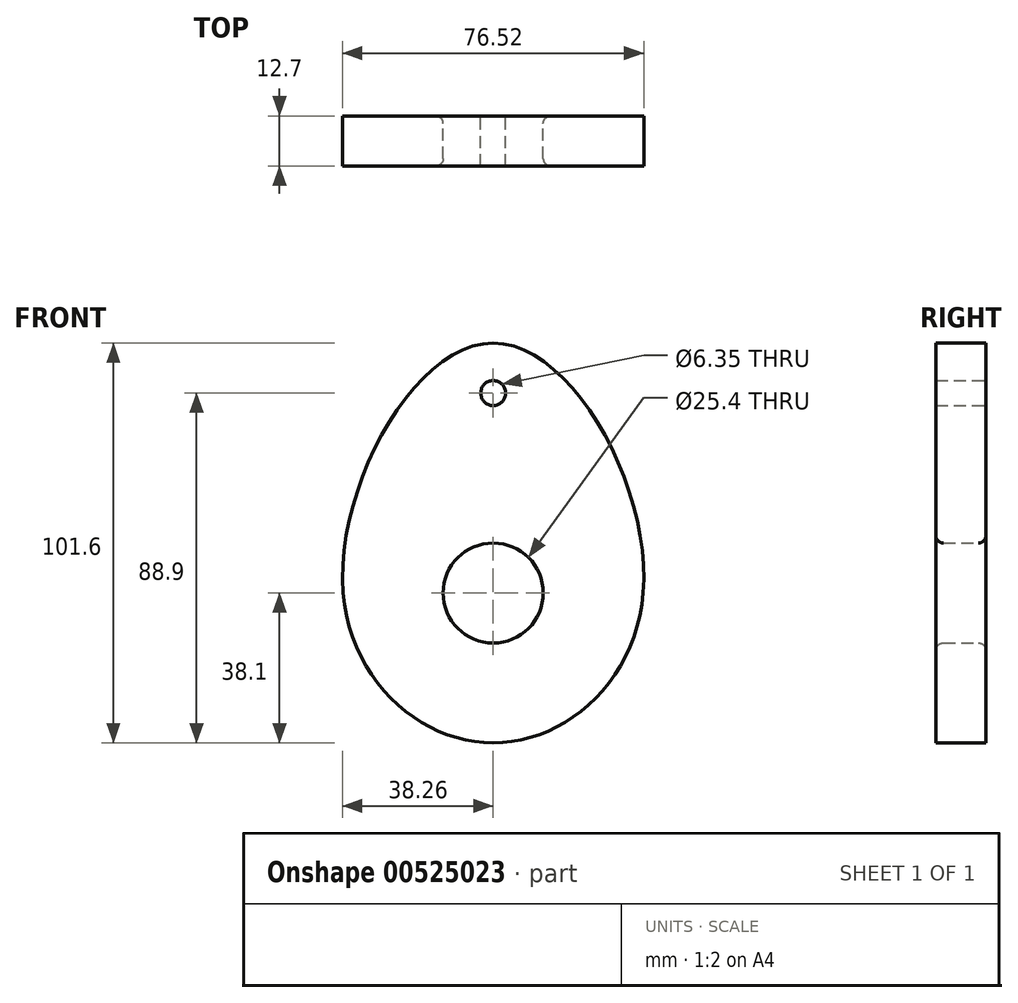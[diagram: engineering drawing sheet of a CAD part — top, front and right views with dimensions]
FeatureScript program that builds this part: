
annotation { "Feature Type Name" : "Feature", "Feature Type Description" : "" }
export const myFeature = defineFeature(function(context is Context, id is Id, definition is map)
    precondition{}
    {
        {
            var Q0;
            Q0=qCreatedBy(makeId("Front.planeOp"),FACE);
            var sketch = newSketch(context, id + "F0", { "sketchPlane" : qUnion([Q0])});
            skLineSegment(sketch, "E0", {"start": v(0, 0) * mm, "end": v(38.1, 0) * mm});
            skLineSegment(sketch, "E1", {"start": v(0, 0) * mm, "end": v(-38.1, 0) * mm});
            skLineSegment(sketch, "E2", {"start": v(0, 0) * mm, "end": v(0, -38.1) * mm});
            skLineSegment(sketch, "E3", {"start": v(0, 0) * mm, "end": v(0, 63.5) * mm});
            skFitSpline(sketch, "E4", {"points": [v(0, 63.5) * mm, v(-38.1, 0) * mm, v(0, -38.1) * mm, v(38.1, 0) * mm, v(0, 63.5) * mm]});
            skLineSegment(sketch, "E5", {"start": v(0, 63.5) * mm, "end": v(0, 50.8) * mm});
            skCircle(sketch, "E6", {"center": v(0, 50.8) * mm, "radius": 3.18 * mm});
            skCircle(sketch, "E7", {"center": v(0, 0) * mm, "radius": 12.7 * mm});
            skCircle(sketch, "E8", {"center": v(0, 0) * mm, "radius": 19.05 * mm});
            skLineSegment(sketch, "E9", {"start": v(0, 0) * mm, "end": v(0, 19.05) * mm});
            skLineSegment(sketch, "E10", {"start": v(0, 0) * mm, "end": v(4.93, 18.4) * mm});
            skLineSegment(sketch, "E11", {"start": v(0, 0) * mm, "end": v(9.52, 16.5) * mm});
            skLineSegment(sketch, "E12", {"start": v(0, 0) * mm, "end": v(13.47, 13.47) * mm});
            skLineSegment(sketch, "E13", {"start": v(0, 0) * mm, "end": v(16.5, 9.53) * mm});
            skLineSegment(sketch, "E14", {"start": v(0, 0) * mm, "end": v(18.4, 4.93) * mm});
            skLineSegment(sketch, "E15", {"start": v(0, 0) * mm, "end": v(19.05, 0) * mm});
            skLineSegment(sketch, "E16", {"start": v(0, 0) * mm, "end": v(18.4, -4.93) * mm});
            skLineSegment(sketch, "E17", {"start": v(0, 0) * mm, "end": v(16.5, -9.52) * mm});
            skLineSegment(sketch, "E18", {"start": v(0, 0) * mm, "end": v(13.47, -13.47) * mm});
            skLineSegment(sketch, "E19", {"start": v(0, 0) * mm, "end": v(9.53, -16.5) * mm});
            skLineSegment(sketch, "E20", {"start": v(0, 0) * mm, "end": v(4.93, -18.4) * mm});
            skLineSegment(sketch, "E21", {"start": v(0, 0) * mm, "end": v(0, -19.05) * mm});
            skLineSegment(sketch, "E22", {"start": v(0, 0) * mm, "end": v(-4.93, -18.4) * mm});
            skLineSegment(sketch, "E23", {"start": v(0, 0) * mm, "end": v(-9.52, -16.5) * mm});
            skLineSegment(sketch, "E24", {"start": v(0, 0) * mm, "end": v(-13.47, -13.47) * mm});
            skLineSegment(sketch, "E25", {"start": v(0, 0) * mm, "end": v(-16.5, -9.53) * mm});
            skLineSegment(sketch, "E26", {"start": v(0, 0) * mm, "end": v(-18.4, -4.93) * mm});
            skLineSegment(sketch, "E27", {"start": v(0, 0) * mm, "end": v(-19.05, 0) * mm});
            skLineSegment(sketch, "E28", {"start": v(0, 0) * mm, "end": v(-13.47, 13.47) * mm});
            skLineSegment(sketch, "E29", {"start": v(0, 0) * mm, "end": v(-16.5, 9.52) * mm});
            skLineSegment(sketch, "E30", {"start": v(0, 0) * mm, "end": v(-18.4, 4.93) * mm});
            skLineSegment(sketch, "E31", {"start": v(0, 0) * mm, "end": v(-4.93, 18.4) * mm});
            skLineSegment(sketch, "E32", {"start": v(0, 0) * mm, "end": v(-9.53, 16.5) * mm});
            skSolve(sketch);
        }
        {
            var Q0;
            Q0 = qSketchRegion(id + "F0", true);
            var Q1;
            {var subQ0=sQuery(id+"F0.wireOp",EDGE,"E30");var subQ1=sQuery(id+"F0.wireOp",EDGE,"E7");var subQ2=makeQuery(id+"F0.imprint","INTERSECT",VERTEX,{"derivedFrom":[subQ1,subQ0]});Q1=makeQuery(id+"F0.imprint","IMPRINT",FACE,{"disambiguationData":[TD([[makeQuery(id+"F0.imprint","IMPRINT",EDGE,{"disambiguationData":[TD([[subQ2,-1.0]])],"derivedFrom":subQ1}),-1.0]])]});}
            var Q2;
            {var subQ0=sQuery(id+"F0.wireOp",EDGE,"E28");var subQ1=sQuery(id+"F0.wireOp",EDGE,"E7");var subQ2=makeQuery(id+"F0.imprint","INTERSECT",VERTEX,{"derivedFrom":[subQ1,subQ0]});Q2=makeQuery(id+"F0.imprint","IMPRINT",FACE,{"disambiguationData":[TD([[makeQuery(id+"F0.imprint","IMPRINT",EDGE,{"disambiguationData":[TD([[subQ2,-1.0]])],"derivedFrom":subQ1}),-1.0]])]});}
            var Q3;
            {var subQ0=sQuery(id+"F0.wireOp",EDGE,"E31");var subQ1=sQuery(id+"F0.wireOp",EDGE,"E7");var subQ2=makeQuery(id+"F0.imprint","INTERSECT",VERTEX,{"derivedFrom":[subQ1,subQ0]});Q3=makeQuery(id+"F0.imprint","IMPRINT",FACE,{"disambiguationData":[TD([[makeQuery(id+"F0.imprint","IMPRINT",EDGE,{"disambiguationData":[TD([[subQ2,-1.0]])],"derivedFrom":subQ1}),-1.0]])]});}
            var Q4;
            {var subQ0=sQuery(id+"F0.wireOp",EDGE,"E10");var subQ1=sQuery(id+"F0.wireOp",EDGE,"E7");var subQ2=makeQuery(id+"F0.imprint","INTERSECT",VERTEX,{"derivedFrom":[subQ1,subQ0]});Q4=makeQuery(id+"F0.imprint","IMPRINT",FACE,{"disambiguationData":[TD([[makeQuery(id+"F0.imprint","IMPRINT",EDGE,{"disambiguationData":[TD([[subQ2,-1.0]])],"derivedFrom":subQ1}),-1.0]])]});}
            var Q5;
            {var subQ0=sQuery(id+"F0.wireOp",EDGE,"E12");var subQ1=sQuery(id+"F0.wireOp",EDGE,"E7");var subQ2=makeQuery(id+"F0.imprint","INTERSECT",VERTEX,{"derivedFrom":[subQ1,subQ0]});Q5=makeQuery(id+"F0.imprint","IMPRINT",FACE,{"disambiguationData":[TD([[makeQuery(id+"F0.imprint","IMPRINT",EDGE,{"disambiguationData":[TD([[subQ2,-1.0]])],"derivedFrom":subQ1}),-1.0]])]});}
            var Q6;
            {var subQ0=sQuery(id+"F0.wireOp",EDGE,"E14");var subQ1=sQuery(id+"F0.wireOp",EDGE,"E7");var subQ2=makeQuery(id+"F0.imprint","INTERSECT",VERTEX,{"derivedFrom":[subQ1,subQ0]});Q6=makeQuery(id+"F0.imprint","IMPRINT",FACE,{"disambiguationData":[TD([[makeQuery(id+"F0.imprint","IMPRINT",EDGE,{"disambiguationData":[TD([[subQ2,-1.0]])],"derivedFrom":subQ1}),-1.0]])]});}
            var Q7;
            {var subQ0=sQuery(id+"F0.wireOp",EDGE,"E15");var subQ1=sQuery(id+"F0.wireOp",EDGE,"E7");var subQ2=makeQuery(id+"F0.imprint","INTERSECT",VERTEX,{"derivedFrom":[subQ1,subQ0]});Q7=makeQuery(id+"F0.imprint","IMPRINT",FACE,{"disambiguationData":[TD([[makeQuery(id+"F0.imprint","IMPRINT",EDGE,{"disambiguationData":[TD([[subQ2,1.0]])],"derivedFrom":subQ1}),-1.0]])]});}
            var Q8;
            {var subQ0=sQuery(id+"F0.wireOp",EDGE,"E18");var subQ1=sQuery(id+"F0.wireOp",EDGE,"E7");var subQ2=makeQuery(id+"F0.imprint","INTERSECT",VERTEX,{"derivedFrom":[subQ1,subQ0]});Q8=makeQuery(id+"F0.imprint","IMPRINT",FACE,{"disambiguationData":[TD([[makeQuery(id+"F0.imprint","IMPRINT",EDGE,{"disambiguationData":[TD([[subQ2,-1.0]])],"derivedFrom":subQ1}),-1.0]])]});}
            var Q9;
            {var subQ0=sQuery(id+"F0.wireOp",EDGE,"E20");var subQ1=sQuery(id+"F0.wireOp",EDGE,"E7");var subQ2=makeQuery(id+"F0.imprint","INTERSECT",VERTEX,{"derivedFrom":[subQ1,subQ0]});Q9=makeQuery(id+"F0.imprint","IMPRINT",FACE,{"disambiguationData":[TD([[makeQuery(id+"F0.imprint","IMPRINT",EDGE,{"disambiguationData":[TD([[subQ2,-1.0]])],"derivedFrom":subQ1}),-1.0]])]});}
            var Q10;
            {var subQ0=sQuery(id+"F0.wireOp",EDGE,"E22");var subQ1=sQuery(id+"F0.wireOp",EDGE,"E7");var subQ2=makeQuery(id+"F0.imprint","INTERSECT",VERTEX,{"derivedFrom":[subQ1,subQ0]});Q10=makeQuery(id+"F0.imprint","IMPRINT",FACE,{"disambiguationData":[TD([[makeQuery(id+"F0.imprint","IMPRINT",EDGE,{"disambiguationData":[TD([[subQ2,-1.0]])],"derivedFrom":subQ1}),-1.0]])]});}
            var Q11;
            {var subQ0=sQuery(id+"F0.wireOp",EDGE,"E24");var subQ1=sQuery(id+"F0.wireOp",EDGE,"E7");var subQ2=makeQuery(id+"F0.imprint","INTERSECT",VERTEX,{"derivedFrom":[subQ1,subQ0]});Q11=makeQuery(id+"F0.imprint","IMPRINT",FACE,{"disambiguationData":[TD([[makeQuery(id+"F0.imprint","IMPRINT",EDGE,{"disambiguationData":[TD([[subQ2,-1.0]])],"derivedFrom":subQ1}),-1.0]])]});}
            var Q12;
            {var subQ0=sQuery(id+"F0.wireOp",EDGE,"E26");var subQ1=sQuery(id+"F0.wireOp",EDGE,"E7");var subQ2=makeQuery(id+"F0.imprint","INTERSECT",VERTEX,{"derivedFrom":[subQ1,subQ0]});Q12=makeQuery(id+"F0.imprint","IMPRINT",FACE,{"disambiguationData":[TD([[makeQuery(id+"F0.imprint","IMPRINT",EDGE,{"disambiguationData":[TD([[subQ2,-1.0]])],"derivedFrom":subQ1}),-1.0]])]});}
            extrude(context, id + "F1", {"entities" : qUnion([Q0, Q1, Q2, Q3, Q4, Q5, Q6, Q7, Q8, Q9, Q10, Q11, Q12]), "depth" : 12.7 * mm, "offsetDistance" : 25.4 * mm});
        }
        {
            var Q0;
            {var subQ0=sQuery(id+"F0.wireOp",EDGE,"E7");Q0=makeQuery(id+"F1.opExtrude","SWEPT_FACE",FACE,{"disambiguationData":[OSD([subQ0]),TDD([makeQuery(id+"F0.imprint","IMPRINT",EDGE,{"disambiguationData":[TD([[makeQuery(id+"F0.imprint","INTERSECT",VERTEX,{"derivedFrom":[subQ0,sQuery(id+"F0.wireOp",EDGE,"E14")]}),-1.0]])],"derivedFrom":subQ0})])]});}
            var Q1;
            {var subQ0=sQuery(id+"F0.wireOp",EDGE,"E7");Q1=makeQuery(id+"F1.opExtrude","SWEPT_FACE",FACE,{"disambiguationData":[OSD([subQ0]),TDD([makeQuery(id+"F0.imprint","IMPRINT",EDGE,{"disambiguationData":[TD([[makeQuery(id+"F0.imprint","INTERSECT",VERTEX,{"derivedFrom":[subQ0,sQuery(id+"F0.wireOp",EDGE,"E15")]}),1.0]])],"derivedFrom":subQ0})])]});}
            var Q2;
            {var subQ0=sQuery(id+"F0.wireOp",EDGE,"E7");Q2=makeQuery(id+"F1.opExtrude","SWEPT_FACE",FACE,{"disambiguationData":[OSD([subQ0]),TDD([makeQuery(id+"F0.imprint","IMPRINT",EDGE,{"disambiguationData":[TD([[makeQuery(id+"F0.imprint","INTERSECT",VERTEX,{"derivedFrom":[subQ0,sQuery(id+"F0.wireOp",EDGE,"E18")]}),-1.0]])],"derivedFrom":subQ0})])]});}
            var Q3;
            {var subQ0=sQuery(id+"F0.wireOp",EDGE,"E7");Q3=makeQuery(id+"F1.opExtrude","SWEPT_FACE",FACE,{"disambiguationData":[OSD([subQ0]),TDD([makeQuery(id+"F0.imprint","IMPRINT",EDGE,{"disambiguationData":[TD([[makeQuery(id+"F0.imprint","INTERSECT",VERTEX,{"derivedFrom":[subQ0,sQuery(id+"F0.wireOp",EDGE,"E10")]}),-1.0]])],"derivedFrom":subQ0})])]});}
            var Q4;
            {var subQ0=sQuery(id+"F0.wireOp",EDGE,"E7");Q4=makeQuery(id+"F1.opExtrude","SWEPT_FACE",FACE,{"disambiguationData":[OSD([subQ0]),TDD([makeQuery(id+"F0.imprint","IMPRINT",EDGE,{"disambiguationData":[TD([[makeQuery(id+"F0.imprint","INTERSECT",VERTEX,{"derivedFrom":[subQ0,sQuery(id+"F0.wireOp",EDGE,"E12")]}),-1.0]])],"derivedFrom":subQ0})])]});}
            var Q5;
            {var subQ0=sQuery(id+"F0.wireOp",EDGE,"E7");Q5=makeQuery(id+"F1.opExtrude","SWEPT_FACE",FACE,{"disambiguationData":[OSD([subQ0]),TDD([makeQuery(id+"F0.imprint","IMPRINT",EDGE,{"disambiguationData":[TD([[makeQuery(id+"F0.imprint","INTERSECT",VERTEX,{"derivedFrom":[subQ0,sQuery(id+"F0.wireOp",EDGE,"E31")]}),-1.0]])],"derivedFrom":subQ0})])]});}
            var Q6;
            {var subQ0=sQuery(id+"F0.wireOp",EDGE,"E7");Q6=makeQuery(id+"F1.opExtrude","SWEPT_FACE",FACE,{"disambiguationData":[OSD([subQ0]),TDD([makeQuery(id+"F0.imprint","IMPRINT",EDGE,{"disambiguationData":[TD([[makeQuery(id+"F0.imprint","INTERSECT",VERTEX,{"derivedFrom":[subQ0,sQuery(id+"F0.wireOp",EDGE,"E28")]}),-1.0]])],"derivedFrom":subQ0})])]});}
            var Q7;
            {var subQ0=sQuery(id+"F0.wireOp",EDGE,"E7");Q7=makeQuery(id+"F1.opExtrude","SWEPT_FACE",FACE,{"disambiguationData":[OSD([subQ0]),TDD([makeQuery(id+"F0.imprint","IMPRINT",EDGE,{"disambiguationData":[TD([[makeQuery(id+"F0.imprint","INTERSECT",VERTEX,{"derivedFrom":[subQ0,sQuery(id+"F0.wireOp",EDGE,"E30")]}),-1.0]])],"derivedFrom":subQ0})])]});}
            var Q8;
            {var subQ0=sQuery(id+"F0.wireOp",EDGE,"E7");Q8=makeQuery(id+"F1.opExtrude","SWEPT_FACE",FACE,{"disambiguationData":[OSD([subQ0]),TDD([makeQuery(id+"F0.imprint","IMPRINT",EDGE,{"disambiguationData":[TD([[makeQuery(id+"F0.imprint","INTERSECT",VERTEX,{"derivedFrom":[subQ0,sQuery(id+"F0.wireOp",EDGE,"E26")]}),-1.0]])],"derivedFrom":subQ0})])]});}
            var Q9;
            {var subQ0=sQuery(id+"F0.wireOp",EDGE,"E7");Q9=makeQuery(id+"F1.opExtrude","SWEPT_FACE",FACE,{"disambiguationData":[OSD([subQ0]),TDD([makeQuery(id+"F0.imprint","IMPRINT",EDGE,{"disambiguationData":[TD([[makeQuery(id+"F0.imprint","INTERSECT",VERTEX,{"derivedFrom":[subQ0,sQuery(id+"F0.wireOp",EDGE,"E24")]}),-1.0]])],"derivedFrom":subQ0})])]});}
            var Q10;
            {var subQ0=sQuery(id+"F0.wireOp",EDGE,"E7");Q10=makeQuery(id+"F1.opExtrude","SWEPT_FACE",FACE,{"disambiguationData":[OSD([subQ0]),TDD([makeQuery(id+"F0.imprint","IMPRINT",EDGE,{"disambiguationData":[TD([[makeQuery(id+"F0.imprint","INTERSECT",VERTEX,{"derivedFrom":[subQ0,sQuery(id+"F0.wireOp",EDGE,"E22")]}),-1.0]])],"derivedFrom":subQ0})])]});}
            var Q11;
            {var subQ0=sQuery(id+"F0.wireOp",EDGE,"E7");Q11=makeQuery(id+"F1.opExtrude","SWEPT_FACE",FACE,{"disambiguationData":[OSD([subQ0]),TDD([makeQuery(id+"F0.imprint","IMPRINT",EDGE,{"disambiguationData":[TD([[makeQuery(id+"F0.imprint","INTERSECT",VERTEX,{"derivedFrom":[subQ0,sQuery(id+"F0.wireOp",EDGE,"E20")]}),-1.0]])],"derivedFrom":subQ0})])]});}
            fillet(context, id + "F2", {"entities" : qUnion([Q0, Q1, Q2, Q3, Q4, Q5, Q6, Q7, Q8, Q9, Q10, Q11]), "radius" : 1.9 * mm, "tangentPropagation" : true, "allowEdgeOverflow" : false});
        }
    });
